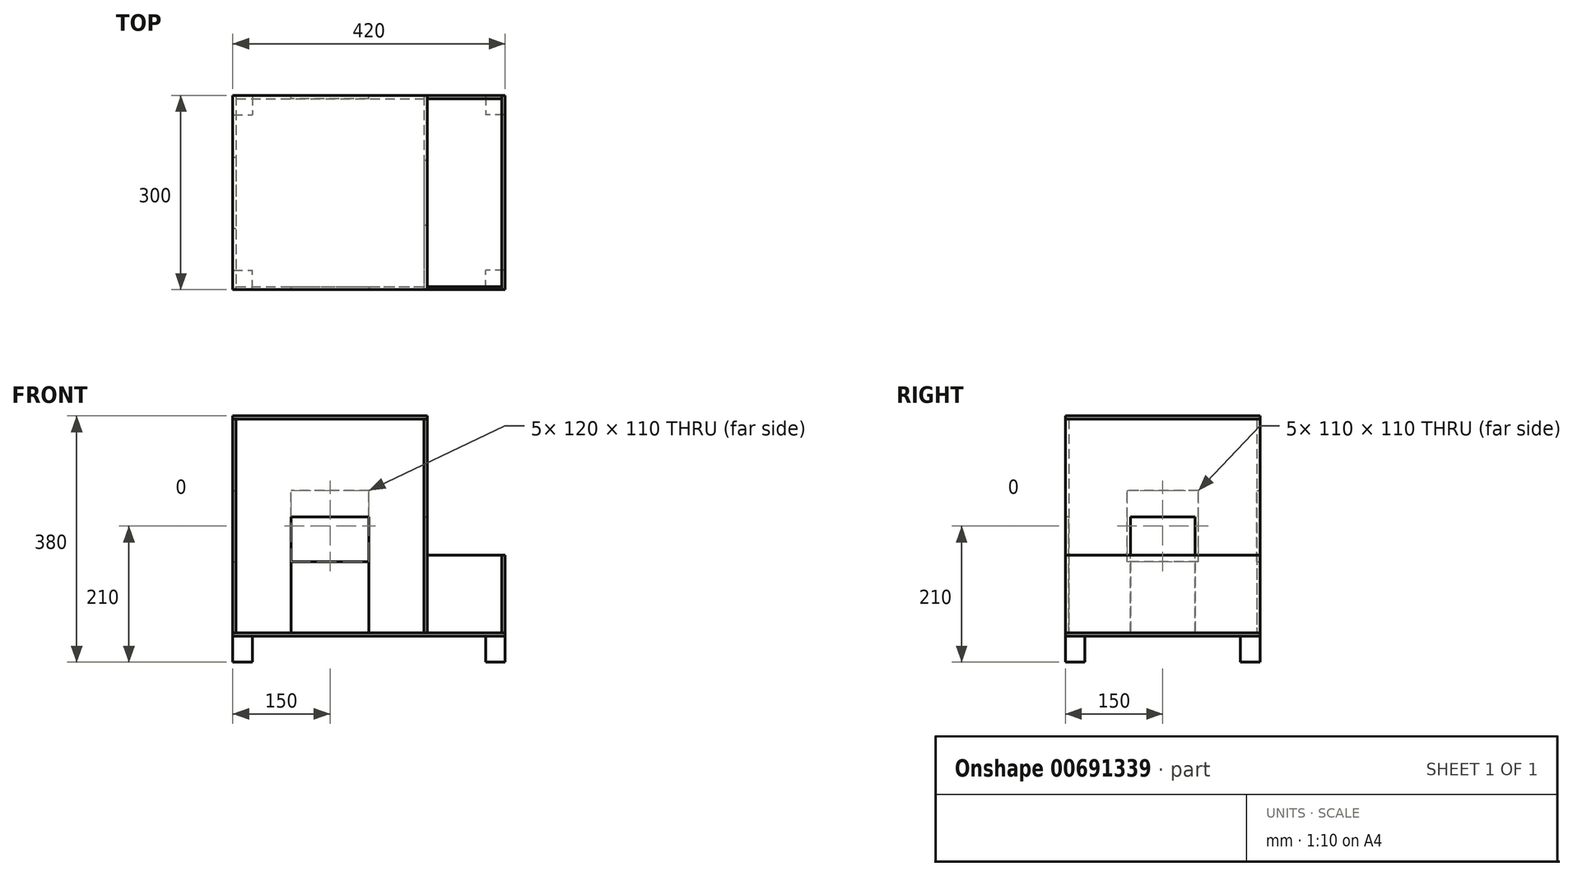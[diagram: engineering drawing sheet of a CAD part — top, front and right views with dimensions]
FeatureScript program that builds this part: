
annotation { "Feature Type Name" : "Feature", "Feature Type Description" : "" }
export const myFeature = defineFeature(function(context is Context, id is Id, definition is map)
    precondition{}
    {
        {
            var Q0;
            Q0=qCreatedBy(makeId("Top.planeOp"),FACE);
            var sketch = newSketch(context, id + "F0", { "sketchPlane" : qUnion([Q0])});
            skLineSegment(sketch, "E0.bottom", {"start": v(210, -150) * mm, "end": v(-210, -150) * mm});
            skLineSegment(sketch, "E0.top", {"start": v(210, 150) * mm, "end": v(-210, 150) * mm});
            skLineSegment(sketch, "E0.left", {"start": v(210, -150) * mm, "end": v(210, 150) * mm});
            skLineSegment(sketch, "E0.right", {"start": v(-210, -150) * mm, "end": v(-210, 150) * mm});
            skPoint(sketch, "E0.middle", {"position": v(0, 0) * mm});
            skSolve(sketch);
        }
        {
            var Q0;
            Q0 = qSketchRegion(id + "F0", true);
            extrude(context, id + "F1", {"entities" : qUnion([Q0]), "depth" : 5 * mm, "offsetDistance" : 25 * mm});
        }
        {
            var Q0;
            Q0=makeQuery(id+"F1.opExtrude","CAP_FACE",FACE,{"disambiguationData":[OSD([sQuery(id+"F0.wireOp",EDGE,"E0.bottom"),sQuery(id+"F0.wireOp",EDGE,"E0.top"),sQuery(id+"F0.wireOp",EDGE,"E0.left"),sQuery(id+"F0.wireOp",EDGE,"E0.right")])],"isStart":true});
            var sketch = newSketch(context, id + "F2", { "sketchPlane" : qUnion([Q0])});
            skLineSegment(sketch, "E1.bottom", {"start": v(-210, 150) * mm, "end": v(-180, 150) * mm});
            skLineSegment(sketch, "E1.top", {"start": v(-210, 120) * mm, "end": v(-180, 120) * mm});
            skLineSegment(sketch, "E1.left", {"start": v(-210, 150) * mm, "end": v(-210, 120) * mm});
            skLineSegment(sketch, "E1.right", {"start": v(-180, 150) * mm, "end": v(-180, 120) * mm});
            skSolve(sketch);
        }
        {
            var Q0;
            Q0 = qSketchRegion(id + "F2", true);
            extrude(context, id + "F3", {"entities" : qUnion([Q0]), "depth" : 40 * mm, "offsetDistance" : 25 * mm});
        }
        {
            var Q0;
            Q0=makeQuery(id+"F3.opExtrude","SWEPT_BODY",BODY,{"disambiguationData":[OSD([sQuery(id+"F2.wireOp",EDGE,"E1.bottom"),sQuery(id+"F2.wireOp",EDGE,"E1.top"),sQuery(id+"F2.wireOp",EDGE,"E1.left"),sQuery(id+"F2.wireOp",EDGE,"E1.right")])]});
            var Q1;
            Q1=qCreatedBy(makeId("Front.planeOp"),FACE);
            mirror(context, id + "F4", {"entities" : qUnion([Q0]), "mirrorPlane" : qUnion([Q1])});
        }
        {
            var Q0;
            Q0=makeQuery(id+"F3.opExtrude","SWEPT_BODY",BODY,{"disambiguationData":[OSD([sQuery(id+"F2.wireOp",EDGE,"E1.bottom"),sQuery(id+"F2.wireOp",EDGE,"E1.top"),sQuery(id+"F2.wireOp",EDGE,"E1.left"),sQuery(id+"F2.wireOp",EDGE,"E1.right")])]});
            var Q1;
            Q1=makeQuery(id+"F4.opPattern","COPY",BODY,{"derivedFrom":makeQuery(id+"F3.opExtrude","SWEPT_BODY",BODY,{"disambiguationData":[OSD([sQuery(id+"F2.wireOp",EDGE,"E1.bottom"),sQuery(id+"F2.wireOp",EDGE,"E1.top"),sQuery(id+"F2.wireOp",EDGE,"E1.left"),sQuery(id+"F2.wireOp",EDGE,"E1.right")])]}),"instanceName":"1"});
            var Q2;
            Q2=qCreatedBy(makeId("Right.planeOp"),FACE);
            mirror(context, id + "F5", {"entities" : qUnion([Q0, Q1]), "mirrorPlane" : qUnion([Q2])});
        }
        {
            var Q0;
            Q0=makeQuery(id+"F1.opExtrude","CAP_FACE",FACE,{"disambiguationData":[OSD([sQuery(id+"F0.wireOp",EDGE,"E0.bottom"),sQuery(id+"F0.wireOp",EDGE,"E0.top"),sQuery(id+"F0.wireOp",EDGE,"E0.left"),sQuery(id+"F0.wireOp",EDGE,"E0.right")])],"isStart":false});
            var sketch = newSketch(context, id + "F6", { "sketchPlane" : qUnion([Q0])});
            skLineSegment(sketch, "E2.bottom", {"start": v(-210, 150) * mm, "end": v(-205, 150) * mm});
            skLineSegment(sketch, "E2.top", {"start": v(-210, -150) * mm, "end": v(-205, -150) * mm});
            skLineSegment(sketch, "E2.left", {"start": v(-210, 150) * mm, "end": v(-210, -150) * mm});
            skLineSegment(sketch, "E2.right", {"start": v(-205, 150) * mm, "end": v(-205, -150) * mm});
            skSolve(sketch);
        }
        {
            var Q0;
            Q0 = qSketchRegion(id + "F6", true);
            extrude(context, id + "F7", {"entities" : qUnion([Q0]), "depth" : 330 * mm, "offsetDistance" : 25 * mm});
        }
        {
            var Q0;
            Q0=makeQuery(id+"F1.opExtrude","CAP_FACE",FACE,{"disambiguationData":[OSD([sQuery(id+"F0.wireOp",EDGE,"E0.bottom"),sQuery(id+"F0.wireOp",EDGE,"E0.top"),sQuery(id+"F0.wireOp",EDGE,"E0.left"),sQuery(id+"F0.wireOp",EDGE,"E0.right")])],"isStart":false});
            var sketch = newSketch(context, id + "F8", { "sketchPlane" : qUnion([Q0])});
            skLineSegment(sketch, "E3.bottom", {"start": v(85, 150) * mm, "end": v(90, 150) * mm});
            skLineSegment(sketch, "E3.top", {"start": v(85, -150) * mm, "end": v(90, -150) * mm});
            skLineSegment(sketch, "E3.left", {"start": v(85, 150) * mm, "end": v(85, -150) * mm});
            skLineSegment(sketch, "E3.right", {"start": v(90, 150) * mm, "end": v(90, -150) * mm});
            skSolve(sketch);
        }
        {
            var Q0;
            Q0 = qSketchRegion(id + "F8", true);
            var Q1;
            Q1=makeQuery(id+"F7.opExtrude","CAP_FACE",FACE,{"disambiguationData":[OSD([sQuery(id+"F6.wireOp",EDGE,"E2.bottom"),sQuery(id+"F6.wireOp",EDGE,"E2.top"),sQuery(id+"F6.wireOp",EDGE,"E2.left"),sQuery(id+"F6.wireOp",EDGE,"E2.right")])],"isStart":false});
            extrude(context, id + "F9", {"entities" : qUnion([Q0]), "endBound" : BoundingType.UP_TO_SURFACE, "depth" : 25 * mm, "endBoundEntityFace" : qUnion([Q1]), "offsetDistance" : 25 * mm});
        }
        {
            var Q0;
            Q0=makeQuery(id+"F1.opExtrude","CAP_FACE",FACE,{"disambiguationData":[OSD([sQuery(id+"F0.wireOp",EDGE,"E0.bottom"),sQuery(id+"F0.wireOp",EDGE,"E0.top"),sQuery(id+"F0.wireOp",EDGE,"E0.left"),sQuery(id+"F0.wireOp",EDGE,"E0.right")])],"isStart":false});
            var sketch = newSketch(context, id + "F10", { "sketchPlane" : qUnion([Q0])});
            skLineSegment(sketch, "E4.bottom", {"start": v(-205, -150) * mm, "end": v(85, -150) * mm});
            skLineSegment(sketch, "E4.top", {"start": v(-205, -145) * mm, "end": v(85, -145) * mm});
            skLineSegment(sketch, "E4.left", {"start": v(-205, -150) * mm, "end": v(-205, -145) * mm});
            skLineSegment(sketch, "E4.right", {"start": v(85, -150) * mm, "end": v(85, -145) * mm});
            skSolve(sketch);
        }
        {
            var Q0;
            Q0 = qSketchRegion(id + "F10", true);
            var Q1;
            Q1=makeQuery(id+"F9.opExtrude","CAP_FACE",FACE,{"disambiguationData":[OSD([sQuery(id+"F8.wireOp",EDGE,"E3.bottom"),sQuery(id+"F8.wireOp",EDGE,"E3.top"),sQuery(id+"F8.wireOp",EDGE,"E3.left"),sQuery(id+"F8.wireOp",EDGE,"E3.right")])],"isStart":false});
            extrude(context, id + "F11", {"entities" : qUnion([Q0]), "endBound" : BoundingType.UP_TO_SURFACE, "depth" : 25 * mm, "endBoundEntityFace" : qUnion([Q1]), "offsetDistance" : 25 * mm});
        }
        {
            var Q0;
            Q0=makeQuery(id+"F11.opExtrude","SWEPT_BODY",BODY,{"disambiguationData":[OSD([sQuery(id+"F10.wireOp",EDGE,"E4.bottom"),sQuery(id+"F10.wireOp",EDGE,"E4.top"),sQuery(id+"F10.wireOp",EDGE,"E4.left"),sQuery(id+"F10.wireOp",EDGE,"E4.right")])]});
            var Q1;
            Q1=qCreatedBy(makeId("Front.planeOp"),FACE);
            mirror(context, id + "F12", {"entities" : qUnion([Q0]), "mirrorPlane" : qUnion([Q1])});
        }
        {
            var Q0;
            Q0=makeQuery(id+"F9.opExtrude","SWEPT_FACE",FACE,{"disambiguationData":[OSD([sQuery(id+"F8.wireOp",EDGE,"E3.right")])]});
            var sketch = newSketch(context, id + "F13", { "sketchPlane" : qUnion([Q0])});
            skLineSegment(sketch, "E5.bottom", {"start": v(-50, 5) * mm, "end": v(50, 5) * mm});
            skLineSegment(sketch, "E5.top", {"start": v(-50, 184) * mm, "end": v(50, 184) * mm});
            skLineSegment(sketch, "E5.left", {"start": v(-50, 5) * mm, "end": v(-50, 184) * mm});
            skLineSegment(sketch, "E5.right", {"start": v(50, 5) * mm, "end": v(50, 184) * mm});
            skLineSegment(sketch, "E6", {"start": v(0, 184) * mm, "end": v(0, 335) * mm, "construction": true});
            skSolve(sketch);
        }
        {
            var Q0;
            Q0 = qSketchRegion(id + "F13", true);
            extrude(context, id + "F14", {"entities" : qUnion([Q0]), "operationType" : NewBodyOperationType.REMOVE, "endBound" : BoundingType.UP_TO_NEXT, "oppositeDirection" : true, "depth" : 25 * mm, "offsetDistance" : 25 * mm});
        }
        {
            var Q0;
            Q0=makeQuery(id+"F1.opExtrude","CAP_FACE",FACE,{"disambiguationData":[OSD([sQuery(id+"F0.wireOp",EDGE,"E0.bottom"),sQuery(id+"F0.wireOp",EDGE,"E0.top"),sQuery(id+"F0.wireOp",EDGE,"E0.left"),sQuery(id+"F0.wireOp",EDGE,"E0.right")])],"isStart":false});
            var sketch = newSketch(context, id + "F15", { "sketchPlane" : qUnion([Q0])});
            skLineSegment(sketch, "E7.bottom", {"start": v(210, -150) * mm, "end": v(205, -150) * mm});
            skLineSegment(sketch, "E7.top", {"start": v(210, 150) * mm, "end": v(205, 150) * mm});
            skLineSegment(sketch, "E7.left", {"start": v(210, -150) * mm, "end": v(210, 150) * mm});
            skLineSegment(sketch, "E7.right", {"start": v(205, -150) * mm, "end": v(205, 150) * mm});
            skSolve(sketch);
        }
        {
            var Q0;
            Q0 = qSketchRegion(id + "F15", true);
            extrude(context, id + "F16", {"entities" : qUnion([Q0]), "depth" : 120 * mm, "offsetDistance" : 25 * mm});
        }
        {
            var Q0;
            Q0=makeQuery(id+"F1.opExtrude","CAP_FACE",FACE,{"disambiguationData":[OSD([sQuery(id+"F0.wireOp",EDGE,"E0.bottom"),sQuery(id+"F0.wireOp",EDGE,"E0.top"),sQuery(id+"F0.wireOp",EDGE,"E0.left"),sQuery(id+"F0.wireOp",EDGE,"E0.right")])],"isStart":false});
            var sketch = newSketch(context, id + "F17", { "sketchPlane" : qUnion([Q0])});
            skLineSegment(sketch, "E8.bottom", {"start": v(90, -150) * mm, "end": v(205, -150) * mm});
            skLineSegment(sketch, "E8.top", {"start": v(90, -145) * mm, "end": v(205, -145) * mm});
            skLineSegment(sketch, "E8.left", {"start": v(90, -150) * mm, "end": v(90, -145) * mm});
            skLineSegment(sketch, "E8.right", {"start": v(205, -150) * mm, "end": v(205, -145) * mm});
            skSolve(sketch);
        }
        {
            var Q0;
            Q0 = qSketchRegion(id + "F17", true);
            var Q1;
            Q1=makeQuery(id+"F16.opExtrude","CAP_FACE",FACE,{"disambiguationData":[OSD([sQuery(id+"F15.wireOp",EDGE,"E7.bottom"),sQuery(id+"F15.wireOp",EDGE,"E7.top"),sQuery(id+"F15.wireOp",EDGE,"E7.left"),sQuery(id+"F15.wireOp",EDGE,"E7.right")])],"isStart":false});
            extrude(context, id + "F18", {"entities" : qUnion([Q0]), "endBound" : BoundingType.UP_TO_SURFACE, "depth" : 25 * mm, "endBoundEntityFace" : qUnion([Q1]), "offsetDistance" : 25 * mm});
        }
        {
            var Q0;
            Q0=makeQuery(id+"F18.opExtrude","SWEPT_BODY",BODY,{"disambiguationData":[OSD([sQuery(id+"F17.wireOp",EDGE,"E8.bottom"),sQuery(id+"F17.wireOp",EDGE,"E8.top"),sQuery(id+"F17.wireOp",EDGE,"E8.left"),sQuery(id+"F17.wireOp",EDGE,"E8.right")])]});
            var Q1;
            Q1=qCreatedBy(makeId("Front.planeOp"),FACE);
            mirror(context, id + "F19", {"entities" : qUnion([Q0]), "mirrorPlane" : qUnion([Q1])});
        }
        {
            var Q0;
            Q0=makeQuery(id+"F7.opExtrude","CAP_FACE",FACE,{"disambiguationData":[OSD([sQuery(id+"F6.wireOp",EDGE,"E2.bottom"),sQuery(id+"F6.wireOp",EDGE,"E2.top"),sQuery(id+"F6.wireOp",EDGE,"E2.left"),sQuery(id+"F6.wireOp",EDGE,"E2.right")])],"isStart":false});
            var sketch = newSketch(context, id + "F20", { "sketchPlane" : qUnion([Q0])});
            skLineSegment(sketch, "E9.bottom", {"start": v(-210, -150) * mm, "end": v(90, -150) * mm});
            skLineSegment(sketch, "E9.top", {"start": v(-210, 150) * mm, "end": v(90, 150) * mm});
            skLineSegment(sketch, "E9.left", {"start": v(-210, -150) * mm, "end": v(-210, 150) * mm});
            skLineSegment(sketch, "E9.right", {"start": v(90, -150) * mm, "end": v(90, 150) * mm});
            skSolve(sketch);
        }
        {
            var Q0;
            Q0 = qSketchRegion(id + "F20", true);
            extrude(context, id + "F21", {"entities" : qUnion([Q0]), "depth" : 5 * mm, "offsetDistance" : 25 * mm});
        }
        {
            var Q0;
            Q0=makeQuery(id+"F11.opExtrude","SWEPT_FACE",FACE,{"disambiguationData":[OSD([sQuery(id+"F10.wireOp",EDGE,"E4.bottom")])]});
            var sketch = newSketch(context, id + "F22", { "sketchPlane" : qUnion([Q0])});
            skLineSegment(sketch, "E10.bottom", {"start": v(-120, 5) * mm, "end": v(0, 5) * mm});
            skLineSegment(sketch, "E10.top", {"start": v(-120, 184) * mm, "end": v(0, 184) * mm});
            skLineSegment(sketch, "E10.left", {"start": v(-120, 5) * mm, "end": v(-120, 184) * mm});
            skLineSegment(sketch, "E10.right", {"start": v(0, 5) * mm, "end": v(0, 184) * mm});
            skLineSegment(sketch, "E11", {"start": v(-60, 184) * mm, "end": v(-60, 335) * mm, "construction": true});
            skSolve(sketch);
        }
        {
            var Q0;
            Q0 = qSketchRegion(id + "F22", true);
            extrude(context, id + "F23", {"entities" : qUnion([Q0]), "operationType" : NewBodyOperationType.REMOVE, "endBound" : BoundingType.UP_TO_NEXT, "oppositeDirection" : true, "depth" : 25 * mm, "offsetDistance" : 25 * mm});
        }
        {
            var Q0;
            Q0=makeQuery(id+"F7.opExtrude","SWEPT_FACE",FACE,{"disambiguationData":[OSD([sQuery(id+"F6.wireOp",EDGE,"E2.right")])]});
            var sketch = newSketch(context, id + "F24", { "sketchPlane" : qUnion([Q0])});
            skLineSegment(sketch, "E12.bottom", {"start": v(55, 115) * mm, "end": v(-55, 115) * mm});
            skLineSegment(sketch, "E12.top", {"start": v(55, 225) * mm, "end": v(-55, 225) * mm});
            skLineSegment(sketch, "E12.left", {"start": v(55, 115) * mm, "end": v(55, 225) * mm});
            skLineSegment(sketch, "E12.right", {"start": v(-55, 115) * mm, "end": v(-55, 225) * mm});
            skLineSegment(sketch, "E13", {"start": v(0, 225) * mm, "end": v(0, 335) * mm, "construction": true});
            skSolve(sketch);
        }
        {
            var Q0;
            Q0 = qSketchRegion(id + "F24", true);
            extrude(context, id + "F25", {"entities" : qUnion([Q0]), "operationType" : NewBodyOperationType.REMOVE, "oppositeDirection" : true, "depth" : 25 * mm, "offsetDistance" : 25 * mm});
        }
        {
            var Q0;
            Q0=makeQuery(id+"F12.opPattern","COPY",FACE,{"derivedFrom":makeQuery(id+"F11.opExtrude","SWEPT_FACE",FACE,{"disambiguationData":[OSD([sQuery(id+"F10.wireOp",EDGE,"E4.bottom")])]}),"instanceName":"1"});
            var sketch = newSketch(context, id + "F26", { "sketchPlane" : qUnion([Q0])});
            skLineSegment(sketch, "E14.bottom", {"start": v(0, 115) * mm, "end": v(120, 115) * mm});
            skLineSegment(sketch, "E14.top", {"start": v(0, 225) * mm, "end": v(120, 225) * mm});
            skLineSegment(sketch, "E14.left", {"start": v(0, 115) * mm, "end": v(0, 225) * mm});
            skLineSegment(sketch, "E14.right", {"start": v(120, 115) * mm, "end": v(120, 225) * mm});
            skLineSegment(sketch, "E15", {"start": v(60, 225) * mm, "end": v(60, 335) * mm, "construction": true});
            skSolve(sketch);
        }
        {
            var Q0;
            Q0 = qSketchRegion(id + "F26", true);
            extrude(context, id + "F27", {"entities" : qUnion([Q0]), "operationType" : NewBodyOperationType.REMOVE, "endBound" : BoundingType.UP_TO_NEXT, "oppositeDirection" : true, "depth" : 25 * mm, "offsetDistance" : 25 * mm});
        }
    });
